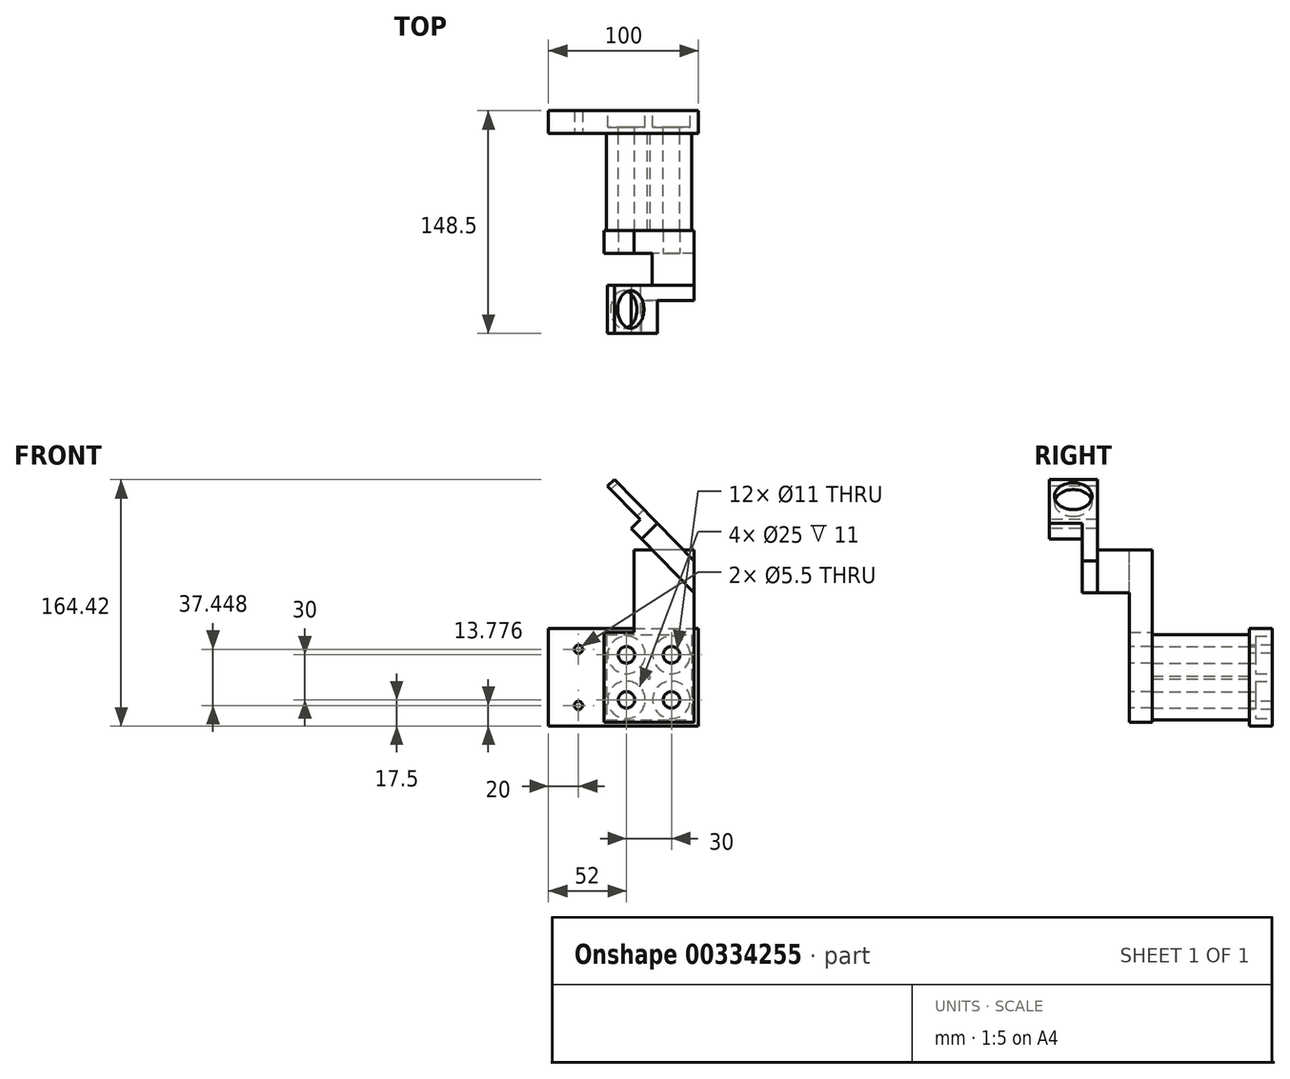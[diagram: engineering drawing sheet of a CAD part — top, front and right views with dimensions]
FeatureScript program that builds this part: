
annotation { "Feature Type Name" : "Feature", "Feature Type Description" : "" }
export const myFeature = defineFeature(function(context is Context, id is Id, definition is map)
    precondition{}
    {
        {
            var Q0;
            Q0=qCreatedBy(makeId("Front.planeOp"),FACE);
            var sketch = newSketch(context, id + "F0", { "sketchPlane" : qUnion([Q0])});
            skLineSegment(sketch, "E0.bottom", {"start": v(-50, 32.5) * mm, "end": v(50, 32.5) * mm});
            skLineSegment(sketch, "E0.top", {"start": v(-50, -32.5) * mm, "end": v(50, -32.5) * mm});
            skLineSegment(sketch, "E0.left", {"start": v(-50, 32.5) * mm, "end": v(-50, -32.5) * mm});
            skLineSegment(sketch, "E0.right", {"start": v(50, 32.5) * mm, "end": v(50, -32.5) * mm});
            skPoint(sketch, "E0.middle", {"position": v(0, 0) * mm});
            skSolve(sketch);
        }
        {
            var Q0;
            Q0 = qSketchRegion(id + "F0", true);
            extrude(context, id + "F1", {"entities" : qUnion([Q0]), "depth" : 15 * mm});
        }
        {
            var Q0;
            Q0=makeQuery(id+"F1.opExtrude","CAP_FACE",FACE,{"disambiguationData":[OSD([sQuery(id+"F0.wireOp",EDGE,"E0.bottom"),sQuery(id+"F0.wireOp",EDGE,"E0.top"),sQuery(id+"F0.wireOp",EDGE,"E0.left"),sQuery(id+"F0.wireOp",EDGE,"E0.right")])],"isStart":false});
            var sketch = newSketch(context, id + "F2", { "sketchPlane" : qUnion([Q0])});
            skPoint(sketch, "E1", {"position": v(-30, 18.72) * mm});
            skPoint(sketch, "E2", {"position": v(-30, -18.72) * mm});
            skPoint(sketch, "E3", {"position": v(-30, 0) * mm});
            skLineSegment(sketch, "E4", {"start": v(-30, 18.72) * mm, "end": v(-30, -18.72) * mm});
            skSolve(sketch);
        }
        {
            var Q0;
            Q0=sQuery(id+"F2.wireOp",VERTEX,"E1");
            var Q1;
            Q1=sQuery(id+"F2.wireOp",VERTEX,"E2");
            var Q2;
            Q2=makeQuery(id+"F1.opExtrude","SWEPT_BODY",BODY,{"disambiguationData":[OSD([sQuery(id+"F0.wireOp",EDGE,"E0.bottom"),sQuery(id+"F0.wireOp",EDGE,"E0.top"),sQuery(id+"F0.wireOp",EDGE,"E0.left"),sQuery(id+"F0.wireOp",EDGE,"E0.right")])]});
            hole(context, id + "F3", {"style" : HoleStyle.SIMPLE, "endStyle" : HoleEndStyle.THROUGH, "standardTappedOrClearance" : lookupTablePath({ "standard" : "ISO", "fit" : "Normal", "size" : "M5", "type" : "Clearance" }), "standardBlindInLast" : lookupTablePath({ "fit" : "Standard", "standard" : "ISO", "size" : "M5", "type" : "Clearance" }), "holeDiameter" : 5.5 * mm, "tappedDepth" : 12 * mm, "tapClearance" : 3, "locations" : qUnion([Q0, Q1]), "scope" : qUnion([Q2])});
        }
        {
            var Q0;
            Q0=makeQuery(id+"F1.opExtrude","CAP_FACE",FACE,{"disambiguationData":[OSD([sQuery(id+"F0.wireOp",EDGE,"E0.bottom"),sQuery(id+"F0.wireOp",EDGE,"E0.top"),sQuery(id+"F0.wireOp",EDGE,"E0.left"),sQuery(id+"F0.wireOp",EDGE,"E0.right")])],"isStart":false});
            var sketch = newSketch(context, id + "F4", { "sketchPlane" : qUnion([Q0])});
            skCircle(sketch, "E5", {"center": v(17, 0) * mm, "radius": 1 * mm});
            skLineSegment(sketch, "E6", {"start": v(-1.39, 0) * mm, "end": v(50, 0) * mm, "construction": true});
            skPoint(sketch, "E7", {"position": v(-30, 18.72) * mm});
            skSolve(sketch);
        }
        {
            var Q0;
            Q0 = qSketchRegion(id + "F4", true);
            extrude(context, id + "F5", {"entities" : qUnion([Q0]), "depth" : 65 * mm});
        }
        {
            var Q0;
            Q0=makeQuery(id+"F5.opExtrude","CAP_FACE",FACE,{"disambiguationData":[OSD([sQuery(id+"F4.wireOp",EDGE,"E5")])],"isStart":false});
            var sketch = newSketch(context, id + "F6", { "sketchPlane" : qUnion([Q0])});
            skLineSegment(sketch, "E8.bottom", {"start": v(-13, 30) * mm, "end": v(7, 30) * mm});
            skLineSegment(sketch, "E8.top", {"start": v(-13, -30) * mm, "end": v(47, -30) * mm});
            skLineSegment(sketch, "E8.left", {"start": v(-13, 30) * mm, "end": v(-13, -30) * mm});
            skLineSegment(sketch, "E8.right", {"start": v(47, 30) * mm, "end": v(47, -30) * mm});
            skPoint(sketch, "E8.middle", {"position": v(17, 0) * mm});
            skLineSegment(sketch, "E9.top", {"start": v(47, 85) * mm, "end": v(7, 85) * mm});
            skLineSegment(sketch, "E9.left", {"start": v(47, 30) * mm, "end": v(47, 85) * mm});
            skLineSegment(sketch, "E9.right", {"start": v(7, 30) * mm, "end": v(7, 85) * mm});
            skSolve(sketch);
        }
        {
            var Q0;
            Q0 = qSketchRegion(id + "F6", true);
            extrude(context, id + "F7", {"entities" : qUnion([Q0]), "depth" : 15 * mm});
        }
        {
            var Q0;
            Q0=makeQuery(id+"F7.opExtrude","CAP_FACE",FACE,{"disambiguationData":[OSD([sQuery(id+"F6.wireOp",EDGE,"E8.bottom"),sQuery(id+"F6.wireOp",EDGE,"E8.top"),sQuery(id+"F6.wireOp",EDGE,"E8.left"),sQuery(id+"F6.wireOp",EDGE,"E8.right"),sQuery(id+"F6.wireOp",EDGE,"E9.top"),sQuery(id+"F6.wireOp",EDGE,"E9.left"),sQuery(id+"F6.wireOp",EDGE,"E9.right")])],"isStart":false});
            var sketch = newSketch(context, id + "F8", { "sketchPlane" : qUnion([Q0])});
            skLineSegment(sketch, "E10", {"start": v(19, 85) * mm, "end": v(47, 85) * mm});
            skLineSegment(sketch, "E11", {"start": v(47, 85) * mm, "end": v(47, 56.43) * mm});
            skLineSegment(sketch, "E12", {"start": v(47, 56.43) * mm, "end": v(19, 85) * mm});
            skSolve(sketch);
        }
        {
            var Q0;
            Q0 = qSketchRegion(id + "F8", true);
            extrude(context, id + "F9", {"entities" : qUnion([Q0]), "operationType" : NewBodyOperationType.ADD, "depth" : 21.5 * mm});
        }
        {
            var Q0;
            Q0=makeQuery(id+"F9.opExtrude","SWEPT_FACE",FACE,{"disambiguationData":[OSD([sQuery(id+"F8.wireOp",EDGE,"E12")])]});
            var sketch = newSketch(context, id + "F10", { "sketchPlane" : qUnion([Q0])});
            skLineSegment(sketch, "E13", {"start": v(116.5, 7.4) * mm, "end": v(116.5, 67.4) * mm});
            skLineSegment(sketch, "E14", {"start": v(116.5, 67.4) * mm, "end": v(148.5, 67.4) * mm});
            skLineSegment(sketch, "E15", {"start": v(148.5, 67.4) * mm, "end": v(148.5, 57.4) * mm});
            skLineSegment(sketch, "E16", {"start": v(148.5, 57.4) * mm, "end": v(126.5, 57.4) * mm});
            skLineSegment(sketch, "E17", {"start": v(126.5, 57.4) * mm, "end": v(126.5, 7.4) * mm});
            skLineSegment(sketch, "E18", {"start": v(126.5, 7.4) * mm, "end": v(116.5, 7.4) * mm});
            skSolve(sketch);
        }
        {
            var Q0;
            Q0 = qSketchRegion(id + "F10", true);
            extrude(context, id + "F11", {"entities" : qUnion([Q0]), "oppositeDirection" : true, "depth" : 15 * mm});
        }
        {
            var Q0;
            Q0=makeQuery(id+"F11.opExtrude","CAP_EDGE",EDGE,{"disambiguationData":[OSD([sQuery(id+"F10.wireOp",EDGE,"E18")])],"isStart":false});
            chamfer(context, id + "F12", {"entities" : qUnion([Q0]), "width" : 15 * mm, "tangentPropagation" : true});
        }
        {
            var Q0;
            Q0=makeQuery(id+"F11.opExtrude","CAP_FACE",FACE,{"disambiguationData":[OSD([sQuery(id+"F10.wireOp",EDGE,"E13"),sQuery(id+"F10.wireOp",EDGE,"E14"),sQuery(id+"F10.wireOp",EDGE,"E15"),sQuery(id+"F10.wireOp",EDGE,"E16"),sQuery(id+"F10.wireOp",EDGE,"E17"),sQuery(id+"F10.wireOp",EDGE,"E18")])],"isStart":false});
            var sketch = newSketch(context, id + "F13", { "sketchPlane" : qUnion([Q0])});
            skLineSegment(sketch, "E19", {"start": v(-116.5, 67.4) * mm, "end": v(-116.5, 98.4) * mm});
            skLineSegment(sketch, "E20", {"start": v(-116.5, 98.4) * mm, "end": v(-148.5, 98.4) * mm});
            skLineSegment(sketch, "E21", {"start": v(-148.5, 98.4) * mm, "end": v(-148.5, 67.4) * mm});
            skLineSegment(sketch, "E22", {"start": v(-116.5, 67.4) * mm, "end": v(-148.5, 98.4) * mm, "construction": true});
            skPoint(sketch, "E23", {"position": v(-132.5, 82.9) * mm});
            skCircle(sketch, "E24", {"center": v(-132.5, 82.9) * mm, "radius": 12.5 * mm});
            skSolve(sketch);
        }
        {
            var Q0;
            Q0=makeQuery(id+"F13.imprint","IMPRINT",FACE,{"disambiguationData":[TD([[makeQuery(id+"F13.imprint","IMPRINT",EDGE,{"derivedFrom":sQuery(id+"F13.wireOp",EDGE,"E19")}),1.0]])]});
            extrude(context, id + "F14", {"entities" : qUnion([Q0]), "operationType" : NewBodyOperationType.ADD, "oppositeDirection" : true, "depth" : 6.5 * mm});
        }
        {
            var Q0;
            Q0=makeQuery(id+"F1.opExtrude","CAP_FACE",FACE,{"disambiguationData":[OSD([sQuery(id+"F0.wireOp",EDGE,"E0.bottom"),sQuery(id+"F0.wireOp",EDGE,"E0.top"),sQuery(id+"F0.wireOp",EDGE,"E0.left"),sQuery(id+"F0.wireOp",EDGE,"E0.right")])],"isStart":true});
            var sketch = newSketch(context, id + "F15", { "sketchPlane" : qUnion([Q0])});
            skLineSegment(sketch, "E25.bottom", {"start": v(-32, 15) * mm, "end": v(-2, 15) * mm});
            skLineSegment(sketch, "E25.top", {"start": v(-32, -15) * mm, "end": v(-2, -15) * mm});
            skLineSegment(sketch, "E25.left", {"start": v(-32, 15) * mm, "end": v(-32, -15) * mm});
            skLineSegment(sketch, "E25.right", {"start": v(-2, 15) * mm, "end": v(-2, -15) * mm});
            skPoint(sketch, "E26", {"position": v(-32, 0) * mm});
            skPoint(sketch, "E27", {"position": v(30, -18.72) * mm});
            skPoint(sketch, "E28", {"position": v(30, 18.72) * mm});
            skSolve(sketch);
        }
        {
            var Q0;
            Q0=sQuery(id+"F15.wireOp",VERTEX,"E25.left.start");
            var Q1;
            Q1=sQuery(id+"F15.wireOp",VERTEX,"E25.right.start");
            var Q2;
            Q2=sQuery(id+"F15.wireOp",VERTEX,"E25.right.end");
            var Q3;
            Q3=sQuery(id+"F15.wireOp",VERTEX,"E25.top.start");
            var Q4;
            Q4=makeQuery(id+"F1.opExtrude","SWEPT_BODY",BODY,{"disambiguationData":[OSD([sQuery(id+"F0.wireOp",EDGE,"E0.bottom"),sQuery(id+"F0.wireOp",EDGE,"E0.top"),sQuery(id+"F0.wireOp",EDGE,"E0.left"),sQuery(id+"F0.wireOp",EDGE,"E0.right")])]});
            hole(context, id + "F16", {"style" : HoleStyle.C_BORE, "endStyle" : HoleEndStyle.BLIND, "standardTappedOrClearance" : lookupTablePath({ "standard" : "ISO", "size" : "11", "type" : "Drilled" }), "standardBlindInLast" : lookupTablePath({ "standard" : "ISO", "size" : "11", "type" : "Drilled" }), "holeDiameter" : 11 * mm, "cBoreDiameter" : 25 * mm, "cBoreDepth" : 11 * mm, "holeDepth" : 20 * mm, "isTappedThrough" : true, "tappedDepth" : 12 * mm, "tapClearance" : 3, "locations" : qUnion([Q0, Q1, Q2, Q3]), "scope" : qUnion([Q4])});
        }
        {
            var Q0;
            Q0=makeQuery(id+"F1.opExtrude","CAP_FACE",FACE,{"disambiguationData":[OSD([sQuery(id+"F0.wireOp",EDGE,"E0.bottom"),sQuery(id+"F0.wireOp",EDGE,"E0.top"),sQuery(id+"F0.wireOp",EDGE,"E0.left"),sQuery(id+"F0.wireOp",EDGE,"E0.right")])],"isStart":false});
            var sketch = newSketch(context, id + "F17", { "sketchPlane" : qUnion([Q0])});
            skLineSegment(sketch, "E29.bottom", {"start": v(-11.5, 28.5) * mm, "end": v(45.5, 28.5) * mm});
            skLineSegment(sketch, "E29.top", {"start": v(-11.5, -28.5) * mm, "end": v(45.5, -28.5) * mm});
            skLineSegment(sketch, "E29.left", {"start": v(-11.5, 28.5) * mm, "end": v(-11.5, -28.5) * mm});
            skLineSegment(sketch, "E29.right", {"start": v(45.5, 28.5) * mm, "end": v(45.5, -28.5) * mm});
            skPoint(sketch, "E29.middle", {"position": v(17, 0) * mm});
            skLineSegment(sketch, "E30", {"start": v(2, 15) * mm, "end": v(32, -15) * mm, "construction": true});
            skSolve(sketch);
        }
        {
            var Q0;
            Q0=makeQuery(id+"F7.opExtrude","CAP_FACE",FACE,{"disambiguationData":[OSD([sQuery(id+"F6.wireOp",EDGE,"E8.bottom"),sQuery(id+"F6.wireOp",EDGE,"E8.top"),sQuery(id+"F6.wireOp",EDGE,"E8.left"),sQuery(id+"F6.wireOp",EDGE,"E8.right"),sQuery(id+"F6.wireOp",EDGE,"E9.top"),sQuery(id+"F6.wireOp",EDGE,"E9.left"),sQuery(id+"F6.wireOp",EDGE,"E9.right")])],"isStart":false});
            var sketch = newSketch(context, id + "F18", { "sketchPlane" : qUnion([Q0])});
            skLineSegment(sketch, "E31.bottom", {"start": v(32, 15) * mm, "end": v(2, 15) * mm});
            skLineSegment(sketch, "E31.top", {"start": v(32, -15) * mm, "end": v(2, -15) * mm});
            skLineSegment(sketch, "E31.left", {"start": v(32, 15) * mm, "end": v(32, -15) * mm});
            skLineSegment(sketch, "E31.right", {"start": v(2, 15) * mm, "end": v(2, -15) * mm});
            skPoint(sketch, "E31.middle", {"position": v(17, 0) * mm});
            skSolve(sketch);
        }
        {
            var Q0;
            Q0=sQuery(id+"F18.wireOp",VERTEX,"E31.left.start");
            var Q1;
            Q1=sQuery(id+"F18.wireOp",VERTEX,"E31.left.end");
            var Q2;
            Q2=sQuery(id+"F18.wireOp",VERTEX,"E31.right.start");
            var Q3;
            Q3=sQuery(id+"F18.wireOp",VERTEX,"E31.right.end");
            var Q4;
            Q4=makeQuery(id+"F7.opExtrude","SWEPT_BODY",BODY,{"disambiguationData":[OSD([sQuery(id+"F6.wireOp",EDGE,"E8.bottom"),sQuery(id+"F6.wireOp",EDGE,"E8.top"),sQuery(id+"F6.wireOp",EDGE,"E8.left"),sQuery(id+"F6.wireOp",EDGE,"E8.right"),sQuery(id+"F6.wireOp",EDGE,"E9.top"),sQuery(id+"F6.wireOp",EDGE,"E9.left"),sQuery(id+"F6.wireOp",EDGE,"E9.right")])]});
            hole(context, id + "F19", {"style" : HoleStyle.SIMPLE, "endStyle" : HoleEndStyle.BLIND, "standardTappedOrClearance" : lookupTablePath({ "standard" : "ISO", "size" : "11", "type" : "Drilled" }), "standardBlindInLast" : lookupTablePath({ "standard" : "ISO", "size" : "11", "type" : "Drilled" }), "holeDiameter" : 11 * mm, "holeDepth" : 20 * mm, "isTappedThrough" : true, "tappedDepth" : 12 * mm, "tapClearance" : 3, "locations" : qUnion([Q0, Q1, Q2, Q3]), "scope" : qUnion([Q4])});
        }
        {
            var Q0;
            Q0=makeQuery(id+"F17.imprint","IMPRINT",FACE,{"disambiguationData":[TD([[makeQuery(id+"F17.imprint","IMPRINT",EDGE,{"derivedFrom":sQuery(id+"F17.wireOp",EDGE,"E29.bottom")}),-1.0]])]});
            extrude(context, id + "F20", {"entities" : qUnion([Q0]), "endBound" : BoundingType.UP_TO_NEXT, "depth" : 25 * mm});
        }
    });
